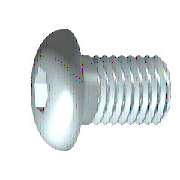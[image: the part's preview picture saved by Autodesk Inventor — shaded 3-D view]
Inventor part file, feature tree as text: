
AUTODESK INVENTOR PART (.ipt)
format: ipt  version: 2016 SP1 (Build 200210100, 210)  size: 198,656 bytes
history: native  units: mm (DEFAULTED — no unit token found)
features: sketch x2, extrude x1, plane x1, fillet x1
ambient origin geometry x7: Origin, YZ Plane, XY Plane, X Axis, Y Axis, Z Axis, Center Point
bodies: Solid1 (feature_tree), Body (feature_tree)
feature tree (5):
  extrude  "Slot"  Depth=1.8542mm
  plane  "Work Plane1"
  fillet  "Fillet2"  Radius=1.8542mm
  sketch  "Sketch1"  dims[d1=4.75976mm d2=1.59014mm d3=1.8542mm]
  sketch  "Sketch2"  dims[d4=1.1176mm d5=60.0deg d6=3.5052mm d7=3.5052mm d8=2.287693mm d9=6.6548mm d10=90.0deg d11=10.0mm d12=0.0mm d13=4.75976mm d14=0.0mm d15=0.486918mm d16=0.486918mm d17=1.6002mm d19=0.0mm d26=6.35mm d27=45.0deg d28=0.0mm d29=0.0mm d30=0.1mm]
